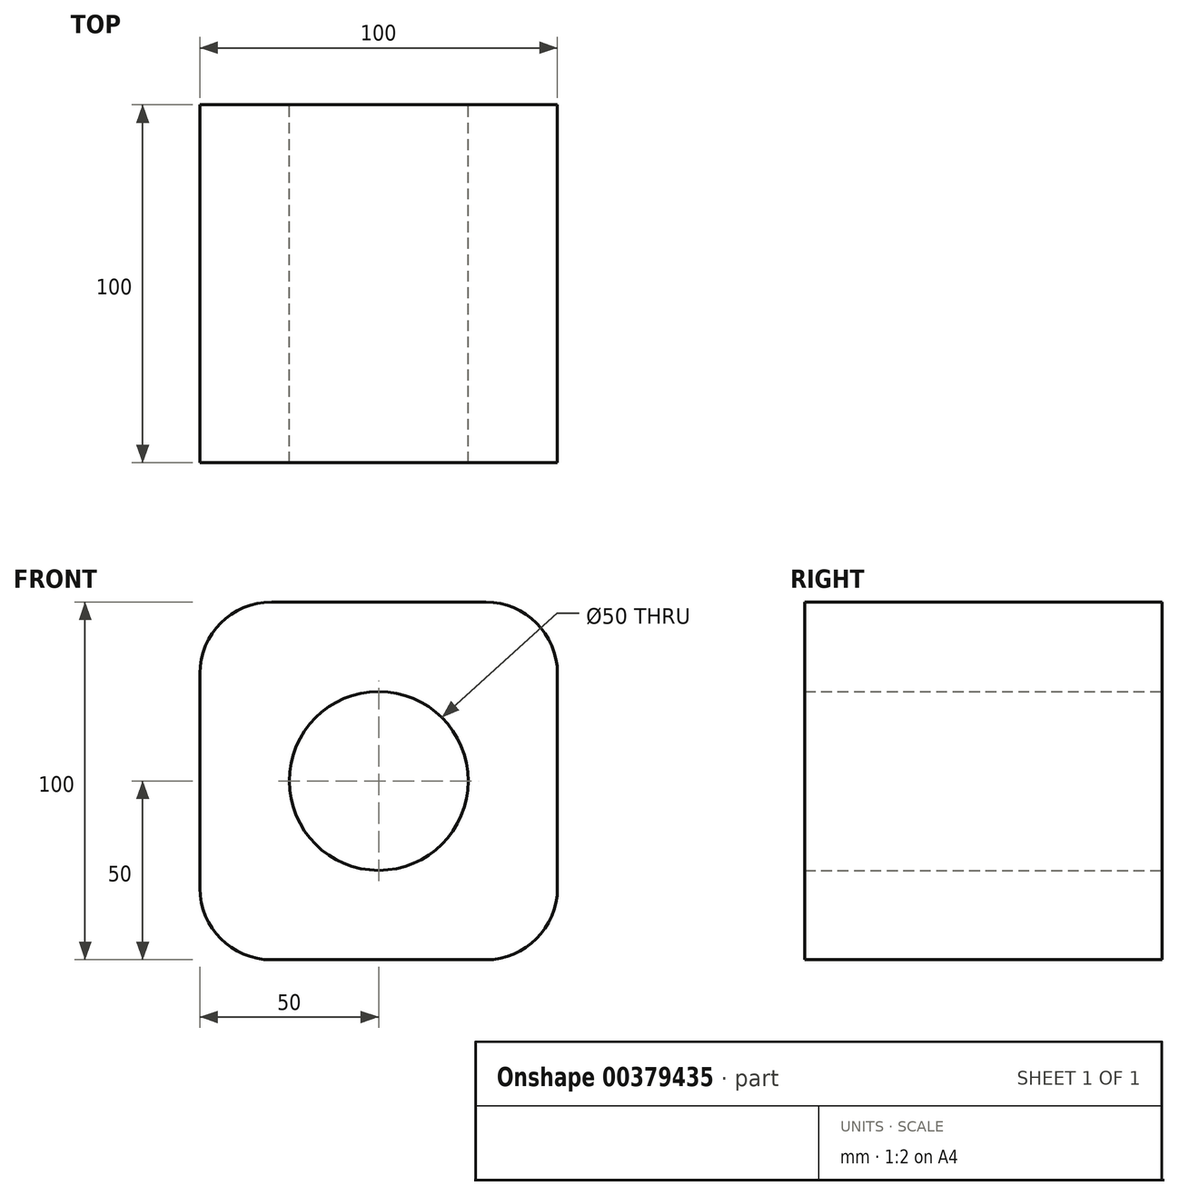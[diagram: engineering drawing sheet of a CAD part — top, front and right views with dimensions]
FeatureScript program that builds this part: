
annotation { "Feature Type Name" : "Feature", "Feature Type Description" : "" }
export const myFeature = defineFeature(function(context is Context, id is Id, definition is map)
    precondition{}
    {
        {
            var Q0;
            Q0=qCreatedBy(makeId("Front.planeOp"),FACE);
            var sketch = newSketch(context, id + "F0", { "sketchPlane" : qUnion([Q0])});
            skLineSegment(sketch, "E0.bottom", {"start": v(30, -50) * mm, "end": v(-30, -50) * mm});
            skLineSegment(sketch, "E0.top", {"start": v(30, 50) * mm, "end": v(-30, 50) * mm});
            skLineSegment(sketch, "E0.left", {"start": v(50, -30) * mm, "end": v(50, 30) * mm});
            skLineSegment(sketch, "E0.right", {"start": v(-50, -30) * mm, "end": v(-50, 30) * mm});
            skPoint(sketch, "E0.middle", {"position": v(0, 0) * mm});
            skPoint(sketch, "E1.visualSharp", {"position": v(-50, 50) * mm});
            skArc(sketch, "E1.filletArc", {"start": v(-30, 50) * mm, "mid": v(-44.14, 44.14) * mm, "end": v(-50, 30) * mm});
            skPoint(sketch, "E2.visualSharp", {"position": v(50, -50) * mm});
            skArc(sketch, "E2.filletArc", {"start": v(30, -50) * mm, "mid": v(44.14, -44.14) * mm, "end": v(50, -30) * mm});
            skPoint(sketch, "E3.visualSharp", {"position": v(50, 50) * mm});
            skArc(sketch, "E3.filletArc", {"start": v(50, 30) * mm, "mid": v(44.14, 44.14) * mm, "end": v(30, 50) * mm});
            skPoint(sketch, "E4.visualSharp", {"position": v(-50, -50) * mm});
            skArc(sketch, "E4.filletArc", {"start": v(-50, -30) * mm, "mid": v(-44.14, -44.14) * mm, "end": v(-30, -50) * mm});
            skCircle(sketch, "E5", {"center": v(0, 0) * mm, "radius": 25 * mm});
            skSolve(sketch);
        }
        {
            var Q0;
            Q0 = qSketchRegion(id + "F0", true);
            extrude(context, id + "F1", {"entities" : qUnion([Q0]), "depth" : 100 * mm});
        }
    });
